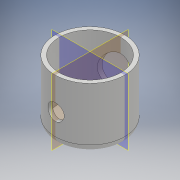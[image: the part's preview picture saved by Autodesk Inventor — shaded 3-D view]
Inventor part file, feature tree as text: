
AUTODESK INVENTOR PART (.ipt)
format: ipt  version: 2017 (Build 210142000, 142)  size: 147,968 bytes
history: native  units: mm
features: extrude x4, sketch x4, fillet x1
ambient origin geometry x8: Origin, YZ Plane, XZ Plane, XY Plane, X Axis, Y Axis, Z Axis, Center Point
bodies: Solid1 (feature_tree)
feature tree (9):
  extrude  "Extrusion1"  Depth=76.0mm
  extrude  "Extrusion2"  Depth=9.0mm
  fillet  "Fillet1"  Radius=20.0mm
  extrude  "Extrusion3"  Depth=35.5mm
  extrude  "Extrusion4"  Depth=35.5mm
  sketch  "Sketch1"  dims[d2=75.0mm d3=0.0mm d4=76.0mm]
  sketch  "Sketch2"  dims[d5=71.0mm d6=0.0mm d7=9.0mm d8=20.0mm]
  sketch  "Sketch3"  dims[d9=10.0mm d10=0.0mm d11=35.5mm]
  sketch  "Sketch6"  dims[d12=44.0mm d13=35.5mm d14=10.0mm d15=0.0mm]
